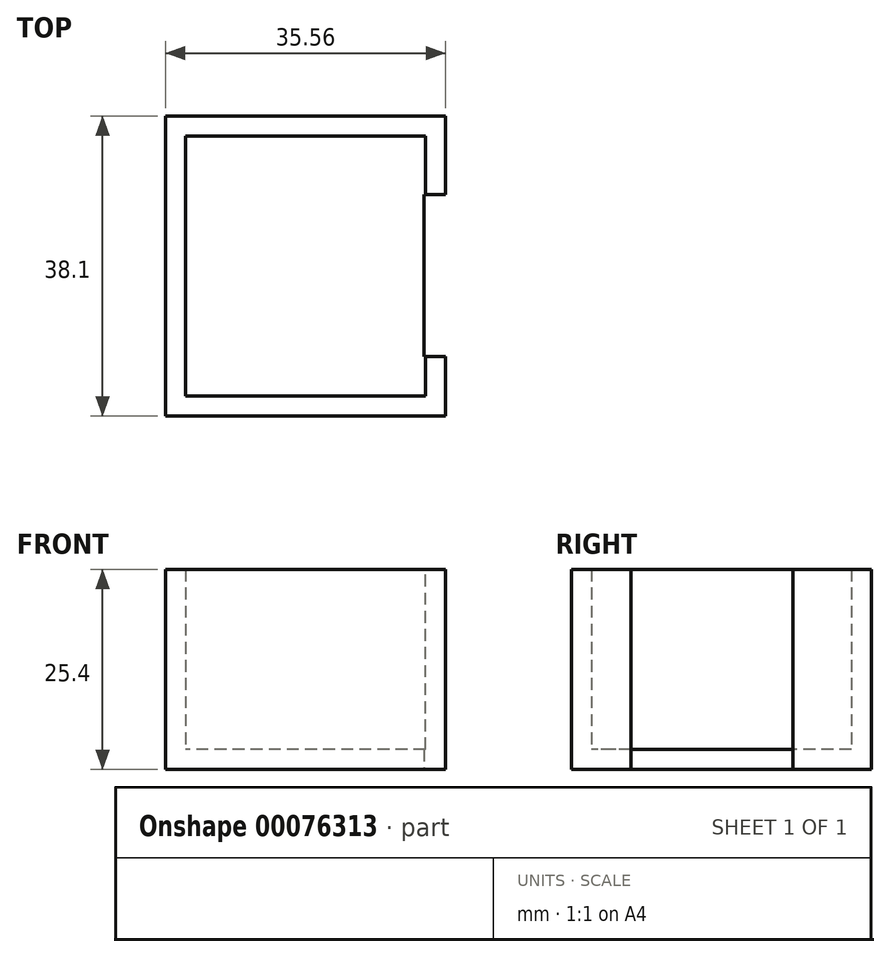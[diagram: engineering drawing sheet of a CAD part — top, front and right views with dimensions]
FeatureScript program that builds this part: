
annotation { "Feature Type Name" : "Feature", "Feature Type Description" : "" }
export const myFeature = defineFeature(function(context is Context, id is Id, definition is map)
    precondition{}
    {
        {
            var Q0;
            Q0=qCreatedBy(makeId("Top.planeOp"),FACE);
            var sketch = newSketch(context, id + "F0", { "sketchPlane" : qUnion([Q0])});
            skLineSegment(sketch, "E0.bottom", {"start": v(17.78, 19.05) * mm, "end": v(-17.78, 19.05) * mm});
            skLineSegment(sketch, "E0.top", {"start": v(17.78, -19.05) * mm, "end": v(-17.78, -19.05) * mm});
            skLineSegment(sketch, "E0.left", {"start": v(17.78, 19.05) * mm, "end": v(17.78, -19.05) * mm});
            skLineSegment(sketch, "E0.right", {"start": v(-17.78, 19.05) * mm, "end": v(-17.78, -19.05) * mm});
            skPoint(sketch, "E0.middle", {"position": v(0, 0) * mm});
            skSolve(sketch);
        }
        {
            var Q0;
            Q0=makeQuery(id+"F0.imprint","IMPRINT",FACE,{"disambiguationData":[TD([[makeQuery(id+"F0.imprint","IMPRINT",EDGE,{"derivedFrom":sQuery(id+"F0.wireOp",EDGE,"E0.bottom")}),1.0]])]});
            extrude(context, id + "F1", {"entities" : qUnion([Q0]), "depth" : 25.4 * mm});
        }
        {
            var Q0;
            Q0=makeQuery(id+"F1.opExtrude","CAP_FACE",FACE,{"disambiguationData":[OSD([sQuery(id+"F0.wireOp",EDGE,"E0.bottom"),sQuery(id+"F0.wireOp",EDGE,"E0.top"),sQuery(id+"F0.wireOp",EDGE,"E0.left"),sQuery(id+"F0.wireOp",EDGE,"E0.right")])],"isStart":false});
            shell(context, id + "F2", {"entities" : qUnion([Q0]), "thickness" : 2.54 * mm});
        }
        {
            var Q0;
            Q0=qCreatedBy(makeId("Top.planeOp"),FACE);
            var sketch = newSketch(context, id + "F3", { "sketchPlane" : qUnion([Q0])});
            skLineSegment(sketch, "E1.bottom", {"start": v(15.03, 9.08) * mm, "end": v(40.43, 9.08) * mm});
            skLineSegment(sketch, "E1.top", {"start": v(15.03, -11.5) * mm, "end": v(40.43, -11.5) * mm});
            skLineSegment(sketch, "E1.left", {"start": v(15.03, 9.08) * mm, "end": v(15.03, -11.5) * mm});
            skLineSegment(sketch, "E1.right", {"start": v(40.43, 9.08) * mm, "end": v(40.43, -11.5) * mm});
            skSolve(sketch);
        }
        {
            var Q0;
            Q0 = qSketchRegion(id + "F3", true);
            extrude(context, id + "F4", {"entities" : qUnion([Q0]), "operationType" : NewBodyOperationType.REMOVE, "depth" : 25.4 * mm});
        }
    });
